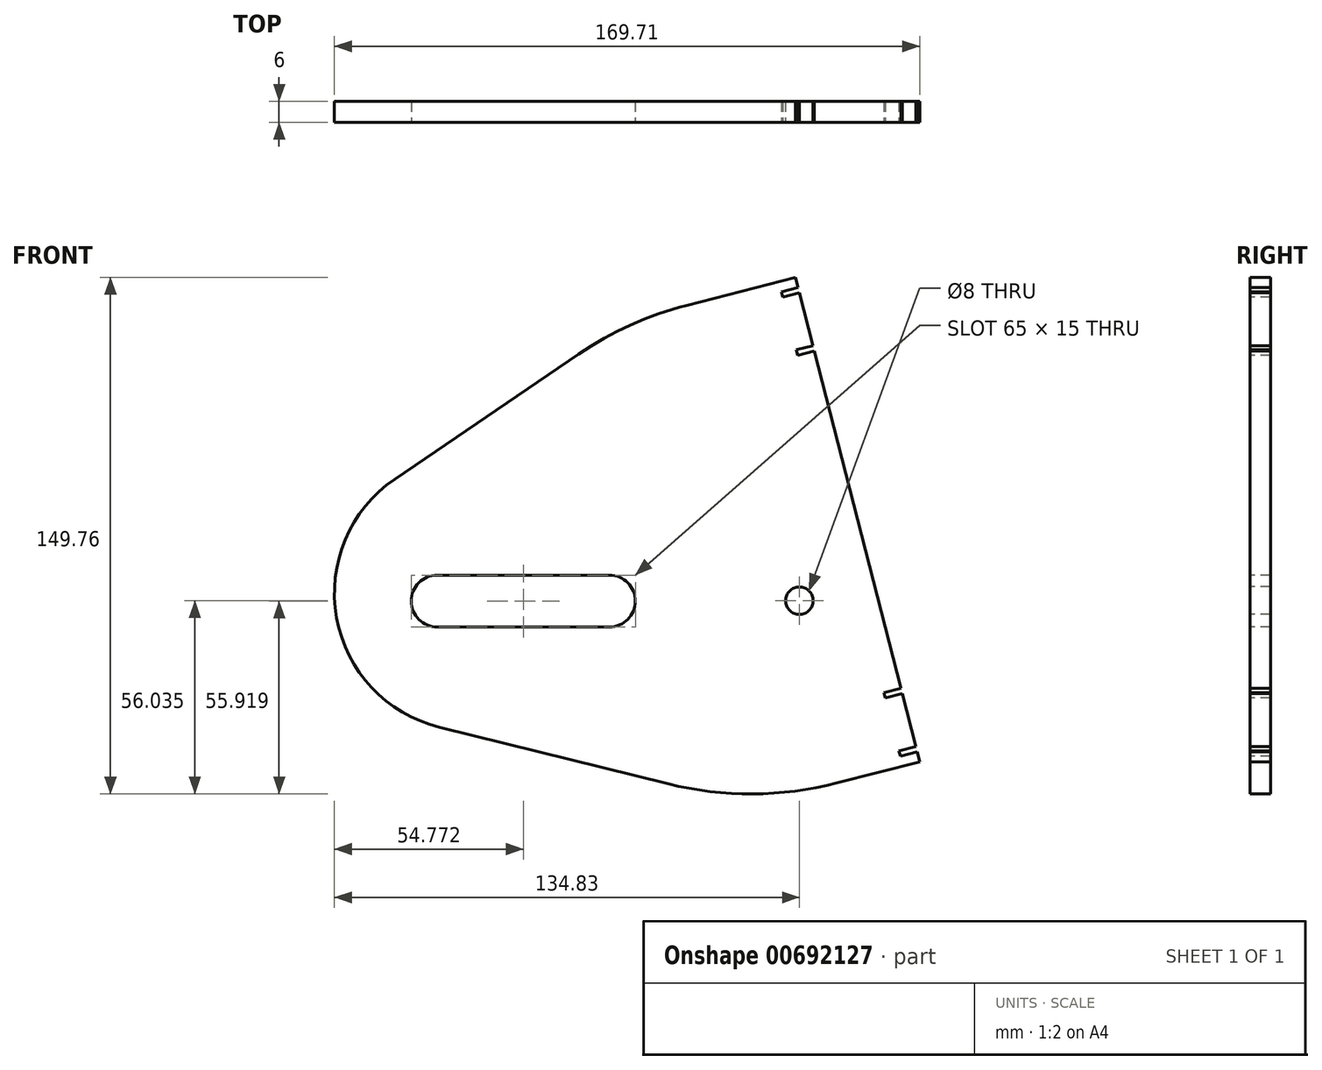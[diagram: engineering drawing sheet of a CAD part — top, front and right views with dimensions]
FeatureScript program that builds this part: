
annotation { "Feature Type Name" : "Feature", "Feature Type Description" : "" }
export const myFeature = defineFeature(function(context is Context, id is Id, definition is map)
    precondition{}
    {
        {
            var Q0;
            Q0=qCreatedBy(makeId("Front.planeOp"),FACE);
            var sketch = newSketch(context, id + "F0", { "sketchPlane" : qUnion([Q0])});
            skLineSegment(sketch, "E0", {"start": v(0, 0) * mm, "end": v(-90, 155.88) * mm});
            skLineSegment(sketch, "E1", {"start": v(0, 0) * mm, "end": v(-173.67, 0) * mm, "construction": true});
            skLineSegment(sketch, "E2", {"start": v(0, 0) * mm, "end": v(215, -372.4) * mm, "construction": true});
            skCircle(sketch, "E3", {"center": v(215, -372.4) * mm, "radius": 295 * mm, "construction": true});
            skLineSegment(sketch, "E4", {"start": v(0, 0) * mm, "end": v(0, -667.4) * mm, "construction": true});
            skLineSegment(sketch, "E5", {"start": v(0, -667.4) * mm, "end": v(-3186.11, -667.4) * mm, "construction": true});
            skLineSegment(sketch, "E6", {"start": v(-3186.11, -667.4) * mm, "end": v(-3186.11, 0) * mm, "construction": true});
            skLineSegment(sketch, "E7", {"start": v(-3186.11, 0) * mm, "end": v(528.5, 0) * mm, "construction": true});
            skCircle(sketch, "E8", {"center": v(-1800, -372.4) * mm, "radius": 295 * mm, "construction": true});
            skLineSegment(sketch, "E9", {"start": v(-45, 77.94) * mm, "end": v(-2085.74, -445.71) * mm, "construction": true});
            skLineSegment(sketch, "E10.0", {"start": v(-76.15, 131.9) * mm, "end": v(-1732.58, -293.15) * mm});
            skLineSegment(sketch, "E11.0", {"start": v(-1679.86, -278.55) * mm, "end": v(-1929.86, -278.55) * mm, "construction": true});
            skLineSegment(sketch, "E12.MirrorCS", {"start": v(-1800, -372.4) * mm, "end": v(-1785.09, -430.5) * mm, "construction": true});
            skLineSegment(sketch, "E13.0", {"start": v(-1804.84, -372.27) * mm, "end": v(-1819.75, -314.16) * mm, "construction": true});
            skLineSegment(sketch, "E14", {"start": v(-1901.57, -398.16) * mm, "end": v(-1901.57, -398.16) * mm});
            skLineSegment(sketch, "E15.0", {"start": v(-1707.98, -348.78) * mm, "end": v(-1722.9, -290.66) * mm});
            skLineSegment(sketch, "E16.MirrorCS", {"start": v(-1707.98, -348.78) * mm, "end": v(-1695.43, -397.7) * mm});
            skPoint(sketch, "E17.visualSharp", {"position": v(-1916.48, -340.05) * mm});
            skPoint(sketch, "E18.visualSharp", {"position": v(-1901.57, -398.16) * mm});
            skPoint(sketch, "E19.visualSharp", {"position": v(-1886.59, -456.55) * mm});
            skLineSegment(sketch, "E20", {"start": v(-1850, -372.4) * mm, "end": v(-1850, -373.27) * mm});
            skLineSegment(sketch, "E21", {"start": v(-1800, -366.4) * mm, "end": v(-1800.01, -366.4) * mm});
            skPoint(sketch, "E22.visualSharp", {"position": v(-1850, -366.4) * mm});
            skPoint(sketch, "E23.visualSharp", {"position": v(-1850, -379.4) * mm});
            skLineSegment(sketch, "E24", {"start": v(-1804.84, -372.27) * mm, "end": v(-1724.84, -372.27) * mm, "construction": true});
            skCircle(sketch, "E25", {"center": v(-1724.84, -372.27) * mm, "radius": 4 * mm});
            skCircle(sketch, "E26", {"center": v(-1817.25, -373.43) * mm, "radius": 100 * mm, "construction": true});
            skLineSegment(sketch, "E27", {"start": v(-2095, -370.92) * mm, "end": v(-1254.85, -374.84) * mm, "construction": true});
            skCircle(sketch, "E28", {"center": v(-1254.85, -374.84) * mm, "radius": 50 * mm, "construction": true});
            skLineSegment(sketch, "E29", {"start": v(-1254.85, -374.84) * mm, "end": v(-1077.93, -374.84) * mm, "construction": true});
            skLineSegment(sketch, "E30", {"start": v(-1077.93, -374.84) * mm, "end": v(-1621.26, -373.13) * mm, "construction": true});
            skLineSegment(sketch, "E31", {"start": v(-1077.93, -374.84) * mm, "end": v(-1077.93, -314.84) * mm, "construction": true});
            skLineSegment(sketch, "E32.0", {"start": v(-1327.93, -372.4) * mm, "end": v(-1327.93, -312.4) * mm});
            skLineSegment(sketch, "E33.0", {"start": v(-1332.77, -373.63) * mm, "end": v(-1332.77, -433.63) * mm});
            skLineSegment(sketch, "E34", {"start": v(-1332.77, -433.63) * mm, "end": v(-1077.93, -374.84) * mm});
            skLineSegment(sketch, "E35", {"start": v(-1327.93, -312.4) * mm, "end": v(-1077.93, -374.84) * mm});
            skLineSegment(sketch, "E36", {"start": v(-1077.93, -374.84) * mm, "end": v(-1077.93, -249.05) * mm});
            skLineSegment(sketch, "E37", {"start": v(-1327.93, -312.4) * mm, "end": v(-1439.28, 121.55) * mm, "construction": true});
            skLineSegment(sketch, "E38", {"start": v(-1357.56, -196.92) * mm, "end": v(-1361.29, -182.39) * mm});
            skLineSegment(sketch, "E39", {"start": v(-1247.84, -325.33) * mm, "end": v(-1808.1, -273.85) * mm, "construction": true});
            skLineSegment(sketch, "E40", {"start": v(-1243.53, -423.54) * mm, "end": v(-1808.52, -473.05) * mm, "construction": true});
            skCircle(sketch, "E41", {"center": v(-1332.77, -433.63) * mm, "radius": 10 * mm});
            skCircle(sketch, "E42", {"center": v(-1327.93, -312.4) * mm, "radius": 10 * mm});
            skCircle(sketch, "E43.0", {"center": v(-1332.77, -433.63) * mm, "radius": 8 * mm});
            skCircle(sketch, "E44.0", {"center": v(-1327.93, -312.4) * mm, "radius": 8 * mm});
            skLineSegment(sketch, "E45", {"start": v(-1357.56, -196.92) * mm, "end": v(-1327.93, -312.4) * mm});
            skLineSegment(sketch, "E46", {"start": v(-1357.56, -196.92) * mm, "end": v(-874.75, -196.92) * mm});
            skLineSegment(sketch, "E47", {"start": v(-13.85, 24) * mm, "end": v(-496.66, 24) * mm});
            skLineSegment(sketch, "E48", {"start": v(-496.66, 24) * mm, "end": v(-874.75, -196.92) * mm});
            skLineSegment(sketch, "E49", {"start": v(-1693.07, -406.9) * mm, "end": v(-1357.56, -196.92) * mm});
            skCircle(sketch, "E50", {"center": v(-1077.93, -374.84) * mm, "radius": 10 * mm});
            skCircle(sketch, "E51.0", {"center": v(-1077.93, -374.84) * mm, "radius": 8 * mm});
            skLineSegment(sketch, "E52", {"start": v(-1327.93, -313.2) * mm, "end": v(-1337.88, -312.29) * mm});
            skPoint(sketch, "E53.visualSharp", {"position": v(-1839.79, -378.83) * mm});
            skPoint(sketch, "E54.visualSharp", {"position": v(-1839.73, -365.4) * mm});
            skPoint(sketch, "E55.visualSharp", {"position": v(-1759.8, -379.58) * mm});
            skPoint(sketch, "E56.newPointA", {"position": v(-1759.73, -367.4) * mm});
            skPoint(sketch, "E56.newPointB", {"position": v(-1759.73, -365.4) * mm});
            skLineSegment(sketch, "E57.0", {"start": v(-1760.01, -372.4) * mm, "end": v(-1760.01, -372.4) * mm});
            skPoint(sketch, "E58.newPointA", {"position": v(-1840.01, -378.4) * mm});
            skPoint(sketch, "E58.newPointB", {"position": v(-1897.97, -377.3) * mm});
            skPoint(sketch, "E59.newPointA", {"position": v(-1840.01, -366.4) * mm});
            skPoint(sketch, "E59.newPointB", {"position": v(-1897.92, -366.4) * mm});
            skPoint(sketch, "E60.newPointA", {"position": v(-1760.01, -366.4) * mm});
            skPoint(sketch, "E60.newPointB", {"position": v(-1250, -366.4) * mm});
            skPoint(sketch, "E61.visualSharp", {"position": v(-1760.01, -372.4) * mm});
            skPoint(sketch, "E62.newPointA", {"position": v(-1250.08, -383.33) * mm});
            skPoint(sketch, "E62.newPointB", {"position": v(-1760.01, -378.4) * mm});
            skLineSegment(sketch, "E63.trimOffspring", {"start": v(-1776.62, -366.4) * mm, "end": v(-1800, -372.4) * mm, "construction": true});
            skLineSegment(sketch, "E64", {"start": v(-1722.9, -290.66) * mm, "end": v(-76.15, 131.9) * mm});
            skLineSegment(sketch, "E65", {"start": v(-13.85, 24) * mm, "end": v(-1693.07, -406.9) * mm});
            skLineSegment(sketch, "E66", {"start": v(-1693.07, -406.9) * mm, "end": v(-1332.77, -433.63) * mm});
            skPoint(sketch, "E67.visualSharp", {"position": v(-1900.1, -367.32) * mm});
            skLineSegment(sketch, "E68.0", {"start": v(-1852.26, -372.65) * mm, "end": v(-1852.26, -372.4) * mm});
            skPoint(sketch, "E69.orphan", {"position": v(-1859.74, -405.28) * mm});
            skPoint(sketch, "E70.end.orphan", {"position": v(-1859.74, -372.02) * mm});
            skPoint(sketch, "E71.visualSharp", {"position": v(-1852.26, -405.65) * mm});
            skPoint(sketch, "E72.visualSharp", {"position": v(-1852.26, -346.85) * mm});
            skPoint(sketch, "E73.orphan", {"position": v(-1852.26, -372.4) * mm});
            skLineSegment(sketch, "E74.0", {"start": v(-1857.26, -372.65) * mm, "end": v(-1857.26, -370.77) * mm});
            skPoint(sketch, "E75.visualSharp", {"position": v(-1857.26, -405.65) * mm});
            skArc(sketch, "E76.converted", {"start": v(-1877.09, -371.26) * mm, "mid": v(-1877.1, -371.6) * mm, "end": v(-1877.1, -371.94) * mm});
            skLineSegment(sketch, "E77", {"start": v(-1829.9, -372.4) * mm, "end": v(-1779.9, -372.4) * mm, "construction": true});
            skLineSegment(sketch, "E78.0", {"start": v(-1829.9, -364.9) * mm, "end": v(-1779.9, -364.9) * mm});
            skLineSegment(sketch, "E79.0", {"start": v(-1829.9, -379.9) * mm, "end": v(-1779.9, -379.9) * mm});
            skArc(sketch, "E80", {"start": v(-1779.9, -379.9) * mm, "mid": v(-1772.4, -372.4) * mm, "end": v(-1779.9, -364.9) * mm});
            skArc(sketch, "E81", {"start": v(-1829.9, -364.9) * mm, "mid": v(-1837.4, -372.4) * mm, "end": v(-1829.9, -379.9) * mm});
            skLineSegment(sketch, "E82.0", {"start": v(-1689.22, -421.75) * mm, "end": v(-1689.26, -421.75) * mm});
            skArc(sketch, "E83.trimOffspring", {"start": v(-1784.65, -420.65) * mm, "mid": v(-1784.54, -420.58) * mm, "end": v(-1784.44, -420.5) * mm});
            skPoint(sketch, "E84.orphan", {"position": v(-1726.52, -415.48) * mm});
            skLineSegment(sketch, "E85.0", {"start": v(-79.26, 144) * mm, "end": v(-1541.04, -231.1) * mm});
            skLineSegment(sketch, "E86.0", {"start": v(-15.59, 10.64) * mm, "end": v(-1513.15, -373.63) * mm});
            skLineSegment(sketch, "E87.0", {"start": v(-1872.65, -391.03) * mm, "end": v(-1877.55, -371.94) * mm});
            skLineSegment(sketch, "E87.1", {"start": v(-1857.73, -449.15) * mm, "end": v(-1854.63, -461.26) * mm});
            skLineSegment(sketch, "E88.trimOffspring", {"start": v(-1726, -278.55) * mm, "end": v(-1726, -278.55) * mm});
            skLineSegment(sketch, "E89.0", {"start": v(-1814.53, -376.12) * mm, "end": v(-1832.55, -305.9) * mm, "construction": true});
            skLineSegment(sketch, "E89.1", {"start": v(-1814.53, -376.12) * mm, "end": v(-1793.24, -459.09) * mm, "construction": true});
            skLineSegment(sketch, "E90.0", {"start": v(-1692.98, -419.2) * mm, "end": v(-1929.6, -419.2) * mm, "construction": true});
            skLineSegment(sketch, "E91", {"start": v(-1817.25, -373.43) * mm, "end": v(-1817.25, -419.2) * mm, "construction": true});
            skLineSegment(sketch, "E92", {"start": v(-1817.25, -419.2) * mm, "end": v(-1817.25, -373.43) * mm, "construction": true});
            skLineSegment(sketch, "E93", {"start": v(-1817.25, -373.43) * mm, "end": v(-1817.25, -314.87) * mm, "construction": true});
            skLineSegment(sketch, "E94.trimOffspring", {"start": v(-1726, -278.55) * mm, "end": v(-1757.5, -286.64) * mm});
            skLineSegment(sketch, "E95.trimOffspring", {"start": v(-1689.96, -419) * mm, "end": v(-1713.99, -425.17) * mm});
            skLineSegment(sketch, "E96.0", {"start": v(-1802.42, -373.01) * mm, "end": v(-1820.44, -302.79) * mm, "construction": true});
            skLineSegment(sketch, "E97.trimOffspring", {"start": v(-1857.73, -449.15) * mm, "end": v(-1886.59, -456.55) * mm});
            skArc(sketch, "E98.trimOffspring", {"start": v(-1877.37, -371.94) * mm, "mid": v(-1877.37, -372.26) * mm, "end": v(-1877.38, -372.6) * mm});
            skLineSegment(sketch, "E99.trimOffspring", {"start": v(-1911, -338.65) * mm, "end": v(-1916.48, -340.05) * mm});
            skLineSegment(sketch, "E100", {"start": v(-1722.9, -290.66) * mm, "end": v(-1724.86, -283) * mm});
            skLineSegment(sketch, "E101", {"start": v(-1725.26, -281.46) * mm, "end": v(-1730.1, -282.7) * mm});
            skLineSegment(sketch, "E102.0", {"start": v(-1724.86, -283) * mm, "end": v(-1729.7, -284.25) * mm});
            skLineSegment(sketch, "E103.0", {"start": v(-76.55, 133.44) * mm, "end": v(-1535.87, -241.02) * mm});
            skLineSegment(sketch, "E104.trimOffspring", {"start": v(-1729.7, -284.25) * mm, "end": v(-1730.1, -282.7) * mm});
            skLineSegment(sketch, "E105.trimOffspring", {"start": v(-1725.25, -281.46) * mm, "end": v(-1726, -278.55) * mm});
            skLineSegment(sketch, "E106.trimOffspring", {"start": v(-1723.3, -289.11) * mm, "end": v(-1724.86, -283) * mm});
            skLineSegment(sketch, "E107.trimOffspring", {"start": v(-1725.25, -281.46) * mm, "end": v(-1725.26, -281.46) * mm});
            skLineSegment(sketch, "E108.MirrorCS", {"start": v(-1720.93, -298.31) * mm, "end": v(-1725.77, -299.56) * mm});
            skLineSegment(sketch, "E109.MirrorCS", {"start": v(-1720.53, -299.86) * mm, "end": v(-1725.38, -301.1) * mm});
            skLineSegment(sketch, "E110.MirrorCS", {"start": v(-1725.77, -299.56) * mm, "end": v(-1725.38, -301.1) * mm});
            skLineSegment(sketch, "E111.MirrorCS", {"start": v(-1695.03, -399.24) * mm, "end": v(-1699.87, -400.49) * mm});
            skLineSegment(sketch, "E112.MirrorCS", {"start": v(-1695.43, -397.7) * mm, "end": v(-1700.27, -398.94) * mm});
            skLineSegment(sketch, "E113.MirrorCS", {"start": v(-1699.87, -400.49) * mm, "end": v(-1700.27, -398.94) * mm});
            skLineSegment(sketch, "E114.MirrorCS", {"start": v(-1691.1, -414.55) * mm, "end": v(-1695.95, -415.8) * mm});
            skLineSegment(sketch, "E115.MirrorCS", {"start": v(-1690.7, -416.1) * mm, "end": v(-1695.55, -417.34) * mm});
            skLineSegment(sketch, "E116.MirrorCS", {"start": v(-1695.95, -415.8) * mm, "end": v(-1695.55, -417.34) * mm});
            skLineSegment(sketch, "E117.trimOffspring", {"start": v(-1690.7, -416.1) * mm, "end": v(-1686.7, -431.75) * mm});
            skLineSegment(sketch, "E118.trimOffspring", {"start": v(-1695.03, -399.24) * mm, "end": v(-1691.1, -414.55) * mm});
            skLineSegment(sketch, "E119.0", {"start": v(-1778.12, -276.6) * mm, "end": v(-1737.72, -434.05) * mm, "construction": true});
            skLineSegment(sketch, "E120", {"start": v(-1738.4, -431.43) * mm, "end": v(-1848.68, -431.43) * mm, "construction": true});
            skLineSegment(sketch, "E121", {"start": v(-1800, -372.4) * mm, "end": v(-2069.08, -407.24) * mm, "construction": true});
            skLineSegment(sketch, "E122", {"start": v(-1726, -278.55) * mm, "end": v(-1730.97, -259.18) * mm, "construction": true});
            skLineSegment(sketch, "E123", {"start": v(-1689.96, -419) * mm, "end": v(-1685, -438.38) * mm, "construction": true});
            skLineSegment(sketch, "E124", {"start": v(-1738.4, -431.43) * mm, "end": v(-1738.4, -228.65) * mm, "construction": true});
            skLineSegment(sketch, "E125", {"start": v(-1788.89, -300.81) * mm, "end": v(-1842.17, -337.05) * mm});
            skLineSegment(sketch, "E126", {"start": v(-1829.27, -408.96) * mm, "end": v(-1762.85, -425.38) * mm});
            skPoint(sketch, "E127.visualSharp", {"position": v(-1916.26, -387.45) * mm});
            skArc(sketch, "E127.filletArc", {"start": v(-1842.17, -337.05) * mm, "mid": v(-1859.05, -377.19) * mm, "end": v(-1829.27, -408.96) * mm});
            skPoint(sketch, "E128.visualSharp", {"position": v(-1774.43, -290.98) * mm});
            skArc(sketch, "E128.filletArc", {"start": v(-1757.5, -286.64) * mm, "mid": v(-1773.8, -292.36) * mm, "end": v(-1788.89, -300.81) * mm});
            skPoint(sketch, "E129.visualSharp", {"position": v(-1738.4, -431.43) * mm});
            skArc(sketch, "E129.filletArc", {"start": v(-1762.85, -425.38) * mm, "mid": v(-1738.4, -428.3) * mm, "end": v(-1713.99, -425.17) * mm});
            skSolve(sketch);
        }
        {
            var Q0;
            Q0=makeQuery(id+"F0.imprint","IMPRINT",FACE,{"disambiguationData":[TD([[makeQuery(id+"F0.imprint","IMPRINT",EDGE,{"derivedFrom":sQuery(id+"F0.wireOp",EDGE,"E15.0")}),1.0]])]});
            extrude(context, id + "F1", {"entities" : qUnion([Q0]), "oppositeDirection" : true, "depth" : 6 * mm, "offsetDistance" : 25 * mm});
        }
    });
